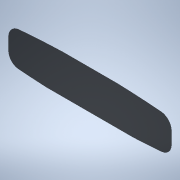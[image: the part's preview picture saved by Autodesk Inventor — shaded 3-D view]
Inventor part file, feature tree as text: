
AUTODESK INVENTOR PART (.ipt)
format: ipt  version: 2021 (Build 250183000, 183)  size: 147,968 bytes
history: native  units: in
note: dims shown in document units (in); Inventor stores cm internally (conversion verified against a paired STEP export)
features: other x3, extrude x1, sketch x1
ambient origin geometry x8: Origin, YZ Plane, XZ Plane, XY Plane, X Axis, Y Axis, Z Axis, Center Point
bodies: Solid1 (feature_tree)
feature tree (5):
  other  "Blocks"
  extrude  "Extrusion1"  Depth=0.0197in
  sketch  "Sketch1"  dims[d0=23.622in d1=4.7244in d2=4.7244in d3=5.5118in d4=5.5118in d5=7.874in d6=7.874in d7=7.874in d8=12.5984in d9=5.6299in d10=0.3937in d11=0.3937in d12=0.5118in d13=0.5118in d14=1.6535in d15=1.5748in d16=1.5748in d17=1.6535in d18=0.7874in d19=11.811in d20=2.9528in d21=0.0197in d22=0.0in]
  other  "Clock Front Face Outline"
  other  "Clock Front Face Outline:1"
